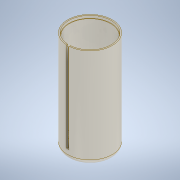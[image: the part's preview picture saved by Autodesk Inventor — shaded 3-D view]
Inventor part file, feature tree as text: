
AUTODESK INVENTOR PART (.ipt)
format: ipt  version: 2020 (Build 240168000, 168)  size: 167,936 bytes
history: native  units: mm
features: sketch x3, extrude x2, revolve x1, fillet x1, projected_geometry x1
ambient origin geometry x8: Origin, YZ Plane, XZ Plane, XY Plane, X Axis, Y Axis, Z Axis, Center Point
bodies: Solid1 (feature_tree)
feature tree (8):
  revolve  "Revolution1"  [1 undecoded]
  extrude  "Extrusion1"  Depth=10.0mm
  fillet  "Fillet1"  Radius=3.5mm
  extrude  "Extrusion2"  Depth=5.0mm
  sketch  "Sketch1"  dims[d0=90.0mm d1=200.0mm]
  sketch  "Sketch2"  dims[d2=10.0mm d5=3.5mm d6=3.5mm]
  projected_geometry  "Projected Loop1"
  sketch  "Sketch3"  dims[d7=90.0deg d8=5.0mm d9=4.4mm d10=180.0mm d11=0.0mm d12=1.0mm d13=85.0mm d14=5.0mm d15=0.0mm]
note: 1 required parameter value undecoded (feature->parameter linkage not recoverable at this tier; creation-order binding heuristic only, values carry confidence <= 0.55)
